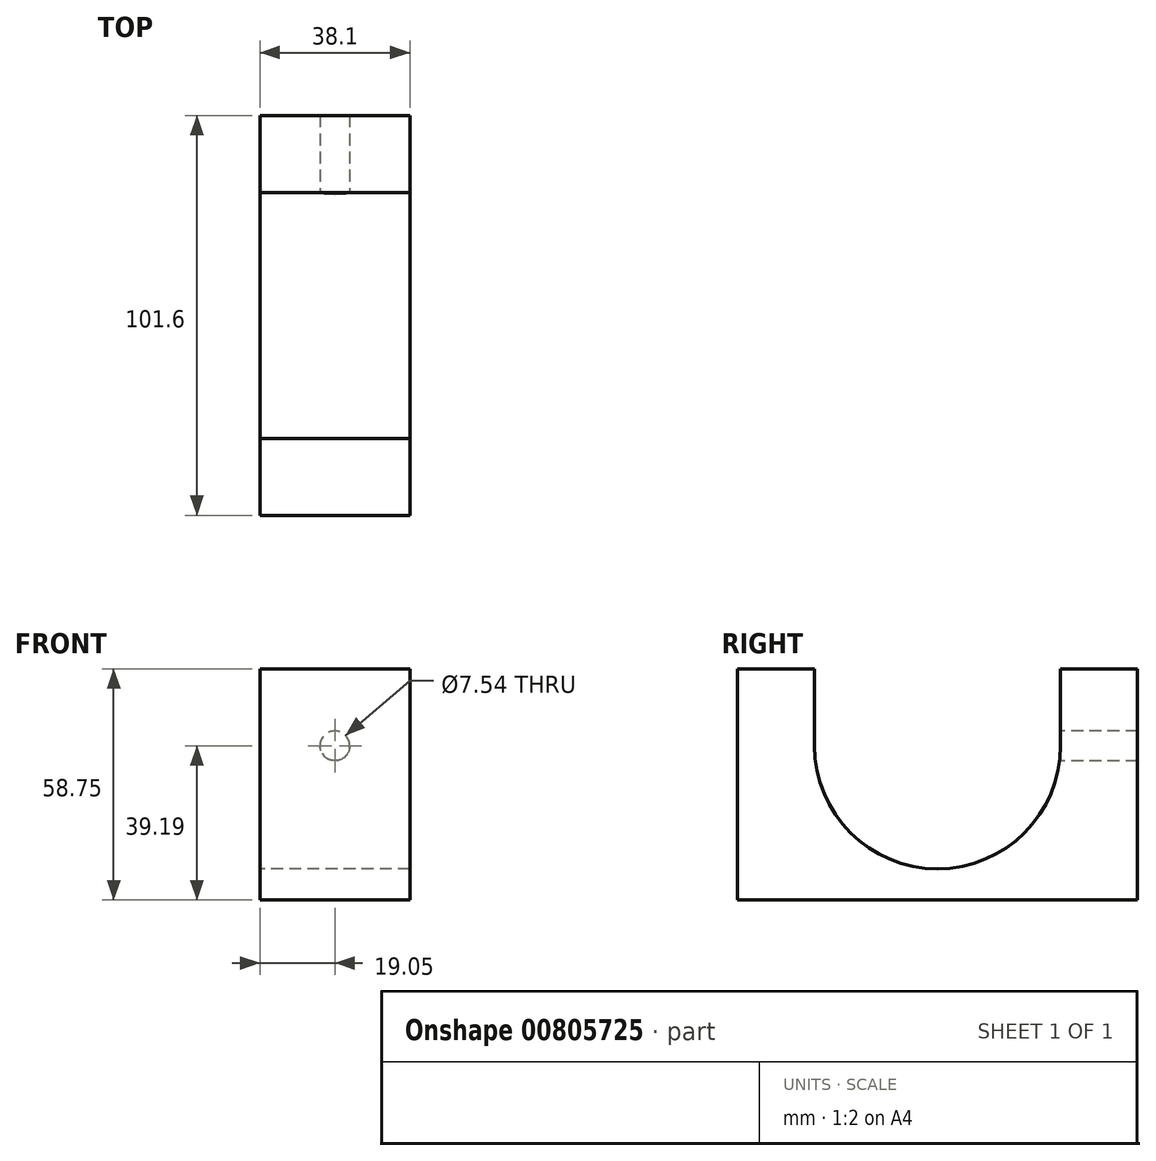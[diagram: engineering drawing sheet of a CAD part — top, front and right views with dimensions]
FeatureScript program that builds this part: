
annotation { "Feature Type Name" : "Feature", "Feature Type Description" : "" }
export const myFeature = defineFeature(function(context is Context, id is Id, definition is map)
    precondition{}
    {
        {
            var Q0;
            Q0=qCreatedBy(makeId("Right.planeOp"),FACE);
            var sketch = newSketch(context, id + "F0", { "sketchPlane" : qUnion([Q0])});
            skCircle(sketch, "E0", {"center": v(0, 0) * mm, "radius": 31.24 * mm});
            skLineSegment(sketch, "E1", {"start": v(50.8, 19.56) * mm, "end": v(50.8, -39.2) * mm});
            skLineSegment(sketch, "E2", {"start": v(50.8, -39.2) * mm, "end": v(0, -39.2) * mm});
            skLineSegment(sketch, "E3", {"start": v(0, -39.2) * mm, "end": v(0, 0) * mm, "construction": true});
            skLineSegment(sketch, "E4.MirrorCS", {"start": v(-50.8, -39.2) * mm, "end": v(0, -39.2) * mm});
            skLineSegment(sketch, "E5.MirrorCS", {"start": v(-50.8, 19.56) * mm, "end": v(-50.8, -39.2) * mm});
            skLineSegment(sketch, "E6", {"start": v(0, 0) * mm, "end": v(31.24, 0) * mm});
            skLineSegment(sketch, "E7", {"start": v(31.24, 0) * mm, "end": v(31.24, 19.56) * mm});
            skLineSegment(sketch, "E8", {"start": v(31.24, 19.56) * mm, "end": v(50.8, 19.56) * mm});
            skLineSegment(sketch, "E9.MirrorCS", {"start": v(-31.24, 0) * mm, "end": v(-31.24, 19.56) * mm});
            skLineSegment(sketch, "E10.MirrorCS", {"start": v(0, 0) * mm, "end": v(-31.24, 0) * mm});
            skLineSegment(sketch, "E11.MirrorCS", {"start": v(-31.24, 19.56) * mm, "end": v(-50.8, 19.56) * mm});
            skSolve(sketch);
        }
        {
            var Q0;
            {var subQ0=sQuery(id+"F0.wireOp",EDGE,"E1");Q0=makeQuery(id+"F0.imprint","IMPRINT",FACE,{"disambiguationData":[TD([[makeQuery(id+"F0.imprint","IMPRINT",EDGE,{"derivedFrom":subQ0}),-1.0]])]});}
            extrude(context, id + "F1", {"entities" : qUnion([Q0]), "depth" : 38.1 * mm, "offsetDistance" : 25.4 * mm, "symmetric" : true});
        }
        {
            var Q0;
            Q0=makeQuery(id+"F1.opExtrude","SWEPT_FACE",FACE,{"disambiguationData":[OSD([sQuery(id+"F0.wireOp",EDGE,"E1")])]});
            var sketch = newSketch(context, id + "F2", { "sketchPlane" : qUnion([Q0])});
            skPoint(sketch, "E12", {"position": v(0, 0) * mm});
            skSolve(sketch);
        }
        {
            var Q0;
            Q0=sQuery(id+"F2.wireOp",VERTEX,"E12");
            var Q1;
            Q1=makeQuery(id+"F1.opExtrude","SWEPT_BODY",BODY,{"disambiguationData":[OSD([sQuery(id+"F0.wireOp",EDGE,"E0"),sQuery(id+"F0.wireOp",EDGE,"E1"),sQuery(id+"F0.wireOp",EDGE,"E2"),sQuery(id+"F0.wireOp",EDGE,"E4.MirrorCS"),sQuery(id+"F0.wireOp",EDGE,"E5.MirrorCS"),sQuery(id+"F0.wireOp",EDGE,"E7"),sQuery(id+"F0.wireOp",EDGE,"E8"),sQuery(id+"F0.wireOp",EDGE,"E9.MirrorCS"),sQuery(id+"F0.wireOp",EDGE,"E11.MirrorCS")])]});
            hole(context, id + "F3", {"style" : HoleStyle.SIMPLE, "endStyle" : HoleEndStyle.BLIND, "standardTappedOrClearance" : lookupTablePath({ "fit" : "Loose (ASME)", "standard" : "ANSI", "size" : "1/4", "type" : "Clearance" }), "standardBlindInLast" : lookupTablePath({ "fit" : "Loose", "standard" : "ANSI", "engagement" : "75%", "pitch" : "20 tpi", "size" : "1/4", "type" : "Clearance & tapped" }), "holeDiameter" : 7.54 * mm, "majorDiameter" : 6.35 * mm, "holeDepth" : 25.4 * mm, "isTappedThrough" : true, "tappedDepth" : 12.7 * mm, "tapClearance" : 3, "locations" : qUnion([Q0]), "scope" : qUnion([Q1]), "startStyle" : HoleStartStyle.SKETCH});
        }
    });
